# Revit family: Quoll Tables
name_source: partatom
category: Furniture
units: mm (PartAtom-declared; Revit-internal decimal feet)

## family parameters
Always vertical = Yes
Cut with Voids When Loaded = No
OmniClass Number = 23.40.20.00
OmniClass Title = General Furniture and Specialties
Room Calculation Point = No
Shared = No
Work Plane-Based = No

## types (4) — shared parameters
Assembly Code = E2020200
Depth = 450 mm  [stored 1.47638 ft]
Foot = Gresham - Black Plastic
Frame = Gresham - BLACK METAL
Manufacturer = Gresham Office Furniture
Range = QUOLL
Table Top = Gresham - CONCRETE
URL = www.gof.co.uk

## per-type parameters (varying)
| type | Height | Width |
| GD27A2 | 455 mm | 915 mm  [stored 3.00197 ft] |
| GD27A1 | 455 mm | 450 mm  [stored 1.47638 ft] |
| GD27B1 | 576 mm  [stored 1.88976 ft] | 450 mm  [stored 1.47638 ft] |
| GD27B2 | 576 mm  [stored 1.88976 ft] | 915 mm  [stored 3.00197 ft] |

note: column(s) folded — value = type name in every type: Product Code

note: [stored X ft] marks values corroborated as IEEE doubles in the binary element streams (Revit-internal decimal feet)

## geometry (parser evidence)
native form markers: Sweep x2
no freeform markers — native parametric forms only
